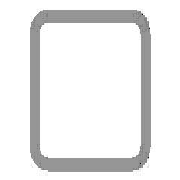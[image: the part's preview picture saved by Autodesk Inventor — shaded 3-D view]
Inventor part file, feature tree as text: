
AUTODESK INVENTOR PART (.ipt)
format: ipt  version: 2025 (Build 290162010, 162A)  size: 134,144 bytes
history: native  units: mm (DEFAULTED — no unit token found)
features: other x4, sketch x1, plane x1
ambient origin geometry x8: Origin, YZ Plane, XZ Plane, XY Plane, X Axis, Y Axis, Z Axis, Center Point
bodies: Solid1 (feature_tree), Body (feature_tree)
feature tree (6):
  parser-record x1  (decoder bookkeeping rows leaked as tree rows — omitted from the tree; the rows remain in map.json)
  other  "Driven Length"
  other  "Start Plane"
  other  "End Plane"
  sketch  "Sketch3"  dims[d3=1720.0mm d4=0.0mm d7=8.0mm d9=60.0mm d11=60.0mm d12=4.0mm d13=-0.0mm d14=1720.0mm d15=30.0mm d16=30.0mm d17=90.0deg d18=1720.0mm]
  plane  "Work Plane3"
